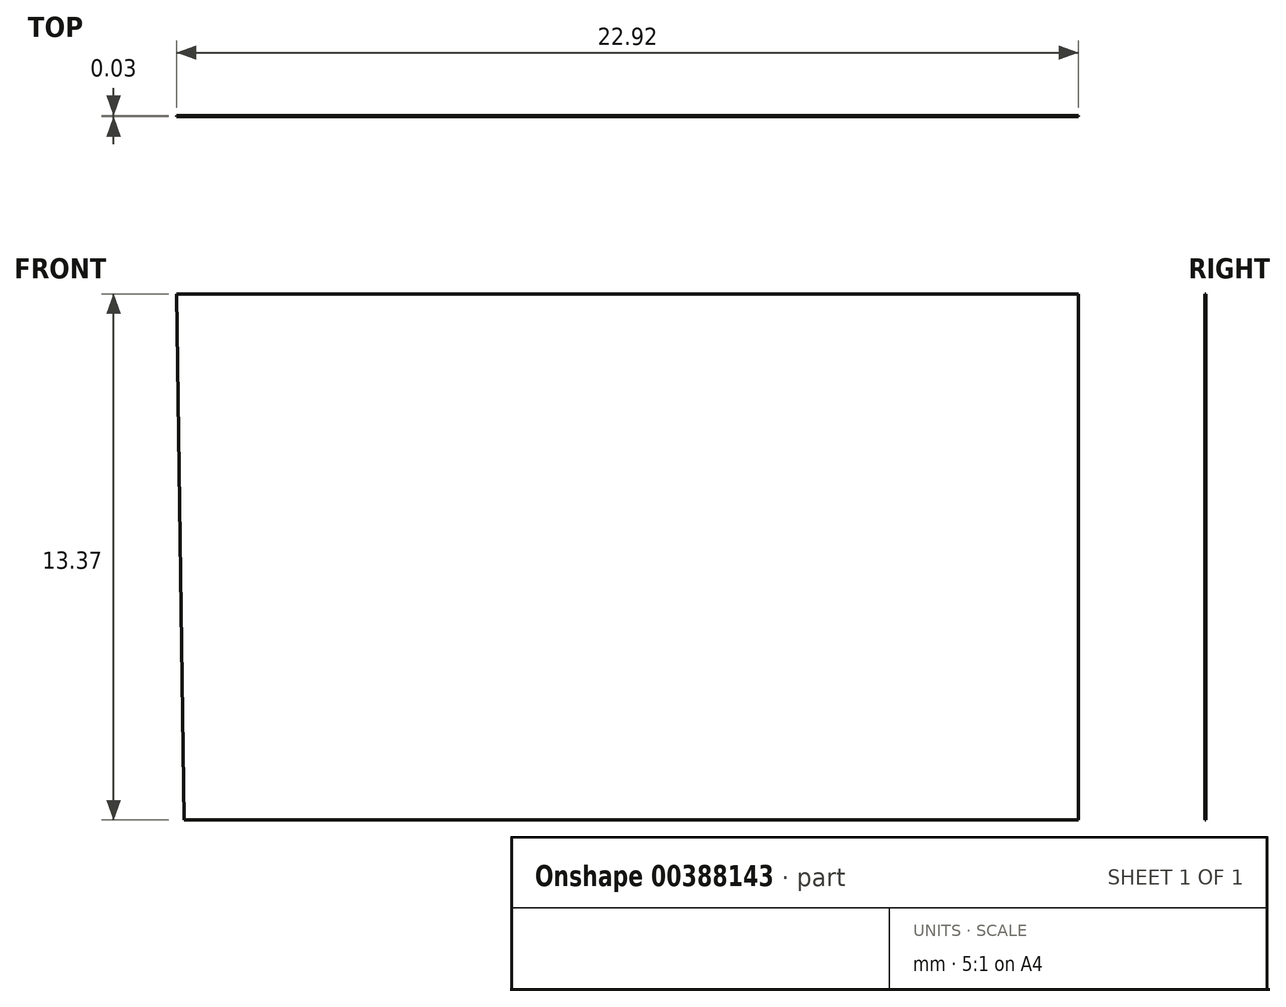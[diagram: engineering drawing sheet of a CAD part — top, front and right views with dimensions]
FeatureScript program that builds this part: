
annotation { "Feature Type Name" : "Feature", "Feature Type Description" : "" }
export const myFeature = defineFeature(function(context is Context, id is Id, definition is map)
    precondition{}
    {
        {
            var Q0;
            Q0=qCreatedBy(makeId("Front.planeOp"),FACE);
            var sketch = newSketch(context, id + "F0", { "sketchPlane" : qUnion([Q0])});
            skLineSegment(sketch, "E0", {"start": v(-60.53, 35.33) * mm, "end": v(-60.53, 21.2) * mm});
            skLineSegment(sketch, "E1", {"start": v(-60.53, 21.2) * mm, "end": v(-41.44, 21.2) * mm});
            skLineSegment(sketch, "E2", {"start": v(-41.44, 21.2) * mm, "end": v(-41.44, 34.94) * mm});
            skLineSegment(sketch, "E3", {"start": v(-41.44, 34.94) * mm, "end": v(-60.53, 35.33) * mm});
            skSolve(sketch);
        }
        {
            var Q0;
            Q0=makeQuery(id+"F0.imprint","IMPRINT",FACE,{"disambiguationData":[TD([[makeQuery(id+"F0.imprint","IMPRINT",EDGE,{"derivedFrom":sQuery(id+"F0.wireOp",EDGE,"E0")}),1.0]])]});
            extrude(context, id + "F1", {"entities" : qUnion([Q0]), "depth" : 0.25 * mm});
        }
        {
            var Q0;
            Q0=qCreatedBy(makeId("Front.planeOp"),FACE);
            var sketch = newSketch(context, id + "F2", { "sketchPlane" : qUnion([Q0])});
            skLineSegment(sketch, "E4", {"start": v(-33.6, 35.7) * mm, "end": v(-10.7, 35.7) * mm});
            skLineSegment(sketch, "E5", {"start": v(-10.7, 35.7) * mm, "end": v(-10.7, 22.34) * mm});
            skLineSegment(sketch, "E6", {"start": v(-10.7, 22.34) * mm, "end": v(-33.42, 22.34) * mm});
            skLineSegment(sketch, "E7", {"start": v(-33.42, 22.34) * mm, "end": v(-33.6, 35.7) * mm});
            skSolve(sketch);
        }
        {
            var Q0;
            Q0=makeQuery(id+"F2.imprint","IMPRINT",FACE,{"disambiguationData":[TD([[makeQuery(id+"F2.imprint","IMPRINT",EDGE,{"derivedFrom":sQuery(id+"F2.wireOp",EDGE,"E4")}),-1.0]])]});
            extrude(context, id + "F3", {"entities" : qUnion([Q0]), "depth" : 0.03 * mm});
        }
        {
            var Q0;
            Q0=makeQuery(id+"F1.opExtrude","SWEPT_BODY",BODY,{"disambiguationData":[OSD([sQuery(id+"F0.wireOp",EDGE,"E0"),sQuery(id+"F0.wireOp",EDGE,"E1"),sQuery(id+"F0.wireOp",EDGE,"E2"),sQuery(id+"F0.wireOp",EDGE,"E3")])]});
            deleteBodies(context, id + "F4", {"entities" : qUnion([Q0])});
        }
    });
